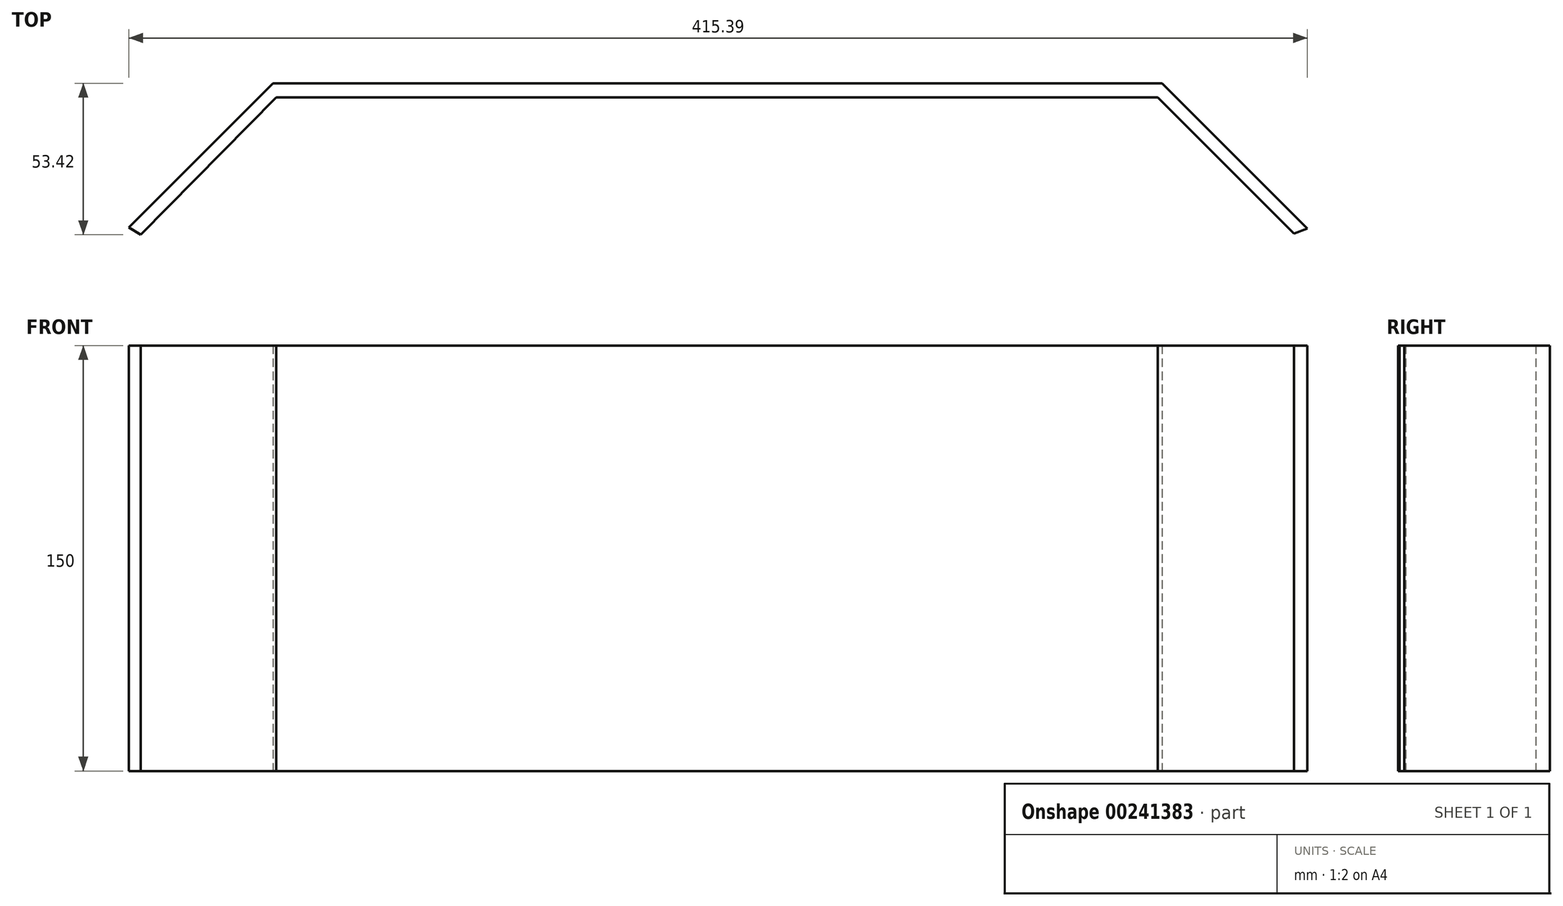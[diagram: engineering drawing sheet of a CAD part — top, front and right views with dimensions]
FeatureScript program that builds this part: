
annotation { "Feature Type Name" : "Feature", "Feature Type Description" : "" }
export const myFeature = defineFeature(function(context is Context, id is Id, definition is map)
    precondition{}
    {
        {
            var Q0;
            Q0=qCreatedBy(makeId("Top.planeOp"),FACE);
            var sketch = newSketch(context, id + "F0", { "sketchPlane" : qUnion([Q0])});
            skLineSegment(sketch, "E0", {"start": v(-126.55, 50) * mm, "end": v(186.75, 50) * mm});
            skSolve(sketch);
        }
        {
            var Q0;
            Q0=qCreatedBy(makeId("Top.planeOp"),FACE);
            var sketch = newSketch(context, id + "F1", { "sketchPlane" : qUnion([Q0])});
            skLineSegment(sketch, "E1", {"start": v(-126.55, 50) * mm, "end": v(-177.37, -0.83) * mm});
            skLineSegment(sketch, "E2", {"start": v(-177.37, -0.83) * mm, "end": v(-173.1, -3.42) * mm});
            skLineSegment(sketch, "E3", {"start": v(-173.1, -3.42) * mm, "end": v(-120.46, 50) * mm});
            skLineSegment(sketch, "E4", {"start": v(186.75, 50) * mm, "end": v(238.02, -1.27) * mm});
            skLineSegment(sketch, "E5", {"start": v(238.02, -1.27) * mm, "end": v(233.31, -2.96) * mm});
            skLineSegment(sketch, "E6", {"start": v(233.31, -2.96) * mm, "end": v(180.2, 50) * mm});
            skLineSegment(sketch, "E7", {"start": v(-126.55, 50) * mm, "end": v(-120.46, 50) * mm});
            skLineSegment(sketch, "E8", {"start": v(180.2, 50) * mm, "end": v(186.75, 50) * mm});
            skLineSegment(sketch, "E9", {"start": v(-125.39, 45) * mm, "end": v(185.22, 45) * mm});
            skLineSegment(sketch, "E10", {"start": v(-120.46, 50) * mm, "end": v(180.2, 50) * mm});
            skSolve(sketch);
        }
        {
            var Q0;
            Q0 = qSketchRegion(id + "F1", true);
            extrude(context, id + "F2", {"entities" : qUnion([Q0]), "depth" : 150 * mm});
        }
    });
